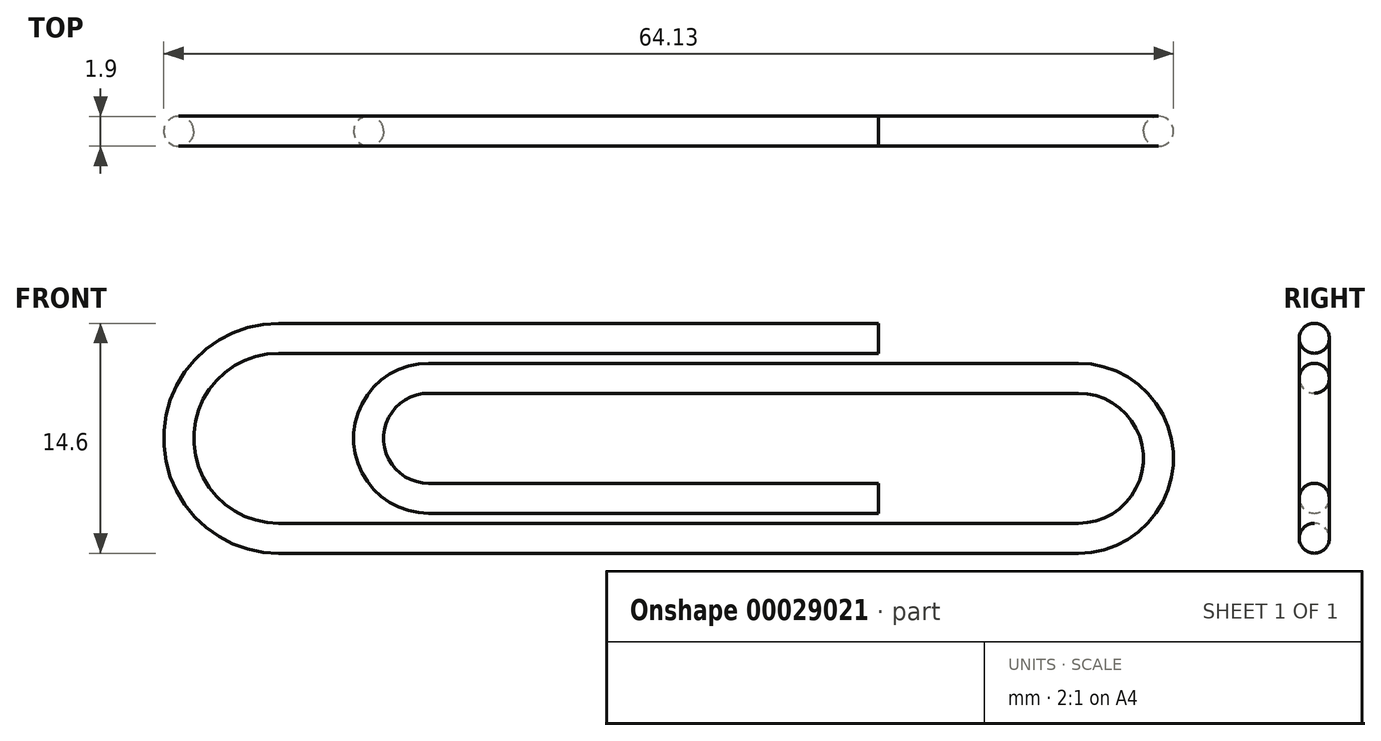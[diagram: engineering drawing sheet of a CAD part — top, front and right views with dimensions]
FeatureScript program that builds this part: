
annotation { "Feature Type Name" : "Feature", "Feature Type Description" : "" }
export const myFeature = defineFeature(function(context is Context, id is Id, definition is map)
    precondition{}
    {
        {
            var Q0;
            Q0=qCreatedBy(makeId("Front.planeOp"),FACE);
            var sketch = newSketch(context, id + "F0", { "sketchPlane" : qUnion([Q0])});
            skArc(sketch, "E0", {"start": v(-50.8, -1.34) * mm, "mid": v(-57.15, -7.7) * mm, "end": v(-50.8, -14.04) * mm});
            skLineSegment(sketch, "E1", {"start": v(-50.8, -1.34) * mm, "end": v(-12.7, -1.34) * mm});
            skLineSegment(sketch, "E2", {"start": v(-50.8, -14.04) * mm, "end": v(0, -14.04) * mm});
            skArc(sketch, "E3", {"start": v(0, -14.04) * mm, "mid": v(5.08, -8.96) * mm, "end": v(0, -3.88) * mm});
            skLineSegment(sketch, "E4", {"start": v(0, -3.88) * mm, "end": v(-41.28, -3.88) * mm});
            skArc(sketch, "E5", {"start": v(-41.28, -3.88) * mm, "mid": v(-45.09, -7.7) * mm, "end": v(-41.28, -11.5) * mm});
            skLineSegment(sketch, "E6", {"start": v(-41.28, -11.5) * mm, "end": v(-12.7, -11.5) * mm});
            skSolve(sketch);
        }
        {
            var Q0;
            Q0=sQuery(id+"F0.wireOp",VERTEX,"E1.end");
            var Q1;
            Q1=sQuery(id+"F0.wireOp",EDGE,"E1");
            cPlane(context, id + "F1", {"entities" : qUnion([Q0, Q1]), "cplaneType" : CPlaneType.LINE_POINT, "offset" : 152.4 * mm, "width" : 152.4 * mm, "height" : 152.4 * mm});
        }
        {
            var Q0;
            Q0=qCreatedBy(id+"F1.planeOp",FACE);
            var sketch = newSketch(context, id + "F2", { "sketchPlane" : qUnion([Q0])});
            skCircle(sketch, "E7", {"center": v(0, -1.34) * mm, "radius": 0.95 * mm});
            skSolve(sketch);
        }
        {
            var Q0;
            Q0=makeQuery(id+"F2.imprint","IMPRINT",FACE,{"disambiguationData":[TD([[makeQuery(id+"F2.imprint","IMPRINT",EDGE,{"derivedFrom":sQuery(id+"F2.wireOp",EDGE,"E7")}),1.0]])]});
            var Q1;
            Q1=sQuery(id+"F2.wireOp",EDGE,"E7");
            var Q2;
            Q2=sQuery(id+"F0.wireOp",EDGE,"E1");
            var Q3;
            Q3=sQuery(id+"F0.wireOp",EDGE,"E0");
            var Q4;
            Q4=sQuery(id+"F0.wireOp",EDGE,"E2");
            var Q5;
            Q5=sQuery(id+"F0.wireOp",EDGE,"E3");
            var Q6;
            Q6=sQuery(id+"F0.wireOp",EDGE,"E4");
            var Q7;
            Q7=sQuery(id+"F0.wireOp",EDGE,"E5");
            var Q8;
            Q8=sQuery(id+"F0.wireOp",EDGE,"E6");
            sweep(context, id + "F3", {"profiles" : qUnion([Q0]), "surfaceProfiles" : qUnion([Q1]), "path" : qUnion([Q2, Q3, Q4, Q5, Q6, Q7, Q8])});
        }
    });
